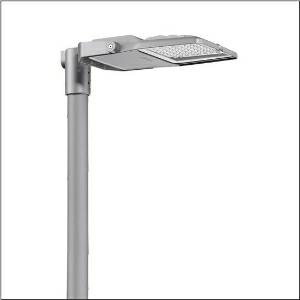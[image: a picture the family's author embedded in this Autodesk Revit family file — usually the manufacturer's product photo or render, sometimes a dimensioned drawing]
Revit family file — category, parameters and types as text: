
# Revit family: floodlight_fl_21_iq_mini___pl43_5xa7771b4a3a_ae81
name_source: partatom
category: Lighting Fixtures
units: mm (PartAtom-declared; Revit-internal decimal feet)

## family parameters
Cut with Voids When Loaded = No
Host = Face
Light Source = No
Part Type = Normal
Room Calculation Point = No
Round Connector Dimension = Use Diameter
Shared = No

## types (1)
- --- (1 x LED, 6660 lm, 45.5 W, 4000K)
    Apparent Load = 46 VA
    CIE Flux Codes = 27 78 99 100 100
    Color Rendering = 70
    Color Temperature = 4000K
    Default Elevation = 1800 mm
    Description = Floodlight FL 21 iQ mini, floodlight, primary light control with lens, of PMMA, primary optical cover: protective disc, of toughened safety glass, transparent, light distribution: PL43, light emission: direct distribution, installation type: surface-mounted, LED, High Power LED, rated luminous flux: 6.660lm, luminous efficacy: 146lm/W, light colour: 740, colour temperature: 4000K, control gear: iQ Comfort/DALI, control: Auto-Match, Temp-Guard, Lumen-Switch, Night-Set, Smart-Wire, Light-Fading, Desk-Remote (wireless, voltage-free reading and setting of iQ features in the workshop via application-optimized NFC function/RFID function), optimised constant luminous flux control (CLO 2.0), with terminal, 6-pole, mains connection: 220..240V, AC, 50/60Hz, start of lifetime: 46W, end of service life: 48W, reduction: 22W, luminaire housing, of diecast aluminium, powder-coated, Siteco® metallic grey (DB 702S), corrosivity category C5 mid according to DIN EN ISO 12944, suitable for swimming pools, chlorine-resistant, sealing non-destructively replaceable, please order mast flange separately, mast bracket, of steel, galvanised, powder-coated, Siteco® metallic grey (DB 702S), protection rating (complete): IP66, insulation class (complete): insulation class II (safety insulation), certification: CE, ENEC, VDE, protection symbol: D, impact resistance: IK08, permissible operating ambient temperature: -40..+40°C, permissible operating ambient temperature for outdoor applications: -40..+50°C, standard: DIN EN 12944, LABS conformity tested according to VDMA 24364:2018-05, packaging unit: 1 piece

Light Distribution: PL43
    Height = 70 mm
    Lamp = 1 x LED
    Lamp Light Flux = 6660 lm
    Lamp Power = 45.5 W
    Lamp count = 1
    Length = 485 mm
    Luminous efficacy = 146 lm/W
    Manufacturer = Siteco
    ModVariant = No
    Model = 5XA7771B4A3A
    Number of Poles = 1
    OnlyDefault = Yes
    Power Factor = 1
    Product Name = Floodlight FL 21 iQ mini | PL43
    Product group = floodlight | pylon annexe
    ProductGroupID = 6200
    Protection Class = Protection class II
    Protection Degree = IP 66
    RLX_Detail_Level = 1
    RLX_Emergency_Light_Flux = 0 lm
    RLX_Emergency_Type = 0
    RLX_Emergency_Type_DB = No
    RlxData = <blob elided: 101161 chars, md5=50b009d0>
    Socket = socket
    Standby Power = 0 W
    System Light Flux = 6660 lm
    System Power = 46 W
    Type Comments = factory setting: luminous flux: 100 % | dim-lin: 254 | 463 mA
    Type Image = l_1007125.jpg
    URL = http://relux.com
    VarID = @adj_162898
    Voltage = 0 V
    Weight = 0.00 kg
    Width = 337 mm

## geometry (parser evidence)
native form markers: Blend x4, Sweep x11
no freeform markers — native parametric forms only
